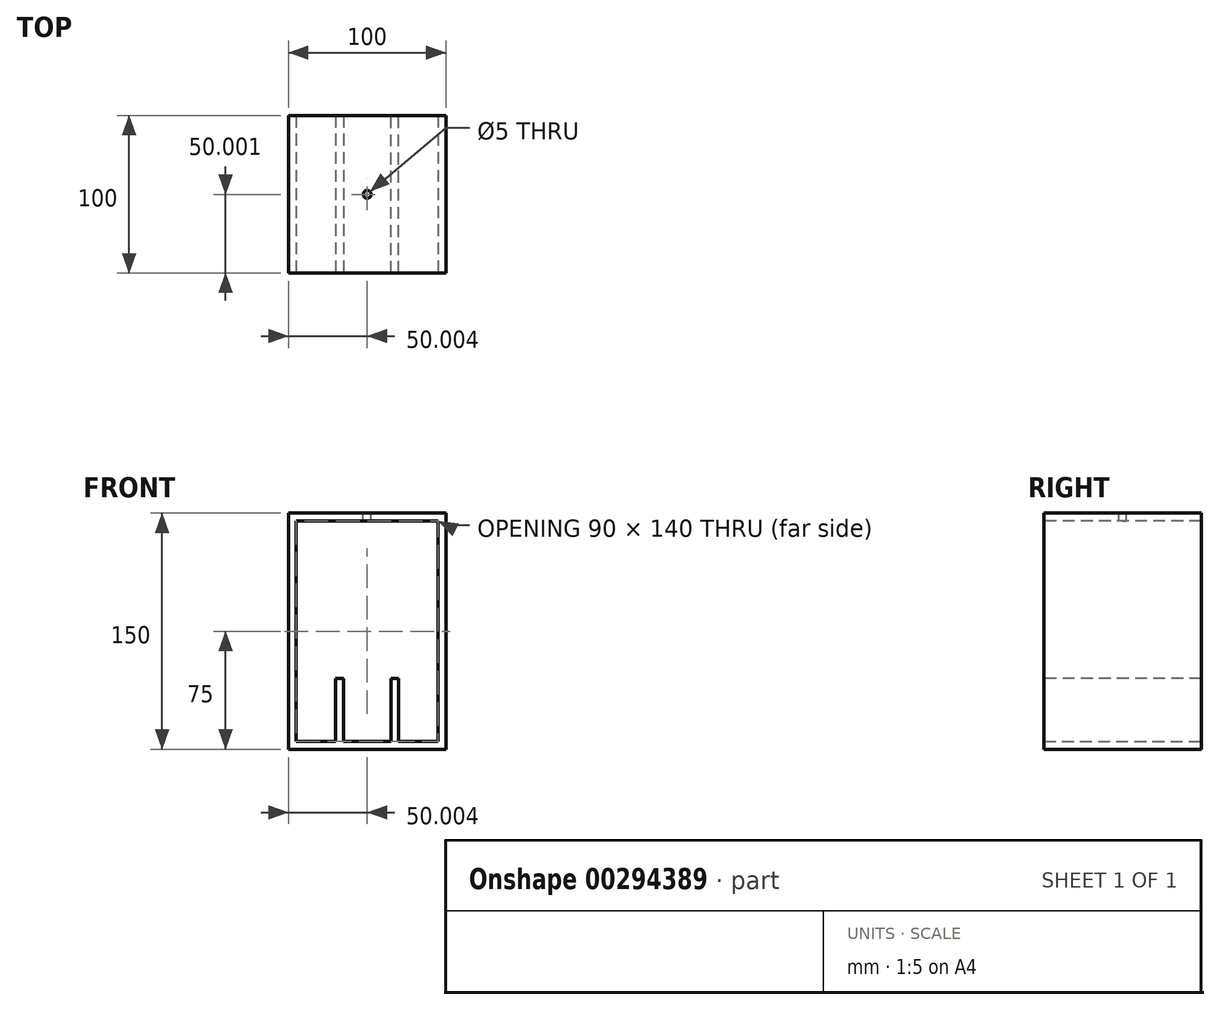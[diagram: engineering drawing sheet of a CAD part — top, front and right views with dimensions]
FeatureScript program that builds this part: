
annotation { "Feature Type Name" : "Feature", "Feature Type Description" : "" }
export const myFeature = defineFeature(function(context is Context, id is Id, definition is map)
    precondition{}
    {
        {
            var Q0;
            Q0=qCreatedBy(makeId("Top.planeOp"),FACE);
            var sketch = newSketch(context, id + "F0", { "sketchPlane" : qUnion([Q0])});
            skLineSegment(sketch, "E0.bottom", {"start": v(-54.99, 57.07) * mm, "end": v(45.01, 57.07) * mm});
            skLineSegment(sketch, "E0.top", {"start": v(-54.99, -42.93) * mm, "end": v(45.01, -42.93) * mm});
            skLineSegment(sketch, "E0.left", {"start": v(-54.99, 57.07) * mm, "end": v(-54.99, -42.93) * mm});
            skLineSegment(sketch, "E0.right", {"start": v(45.01, 57.07) * mm, "end": v(45.01, -42.93) * mm});
            skSolve(sketch);
        }
        {
            var Q0;
            Q0=makeQuery(id+"F0.imprint","IMPRINT",FACE,{"disambiguationData":[TD([[makeQuery(id+"F0.imprint","IMPRINT",EDGE,{"derivedFrom":sQuery(id+"F0.wireOp",EDGE,"E0.bottom")}),-1.0]])]});
            extrude(context, id + "F1", {"entities" : qUnion([Q0]), "depth" : 150 * mm});
        }
        {
            var Q0;
            Q0=makeQuery(id+"F1.opExtrude","SWEPT_FACE",FACE,{"disambiguationData":[OSD([sQuery(id+"F0.wireOp",EDGE,"E0.top")])]});
            var sketch = newSketch(context, id + "F2", { "sketchPlane" : qUnion([Q0])});
            skLineSegment(sketch, "E1.bottom", {"start": v(-49.99, 5) * mm, "end": v(40.01, 5) * mm});
            skLineSegment(sketch, "E1.top", {"start": v(-49.99, 145) * mm, "end": v(40.01, 145) * mm});
            skLineSegment(sketch, "E1.left", {"start": v(-49.99, 5) * mm, "end": v(-49.99, 145) * mm});
            skLineSegment(sketch, "E1.right", {"start": v(40.01, 5) * mm, "end": v(40.01, 145) * mm});
            skSolve(sketch);
        }
        {
            var Q0;
            Q0 = qSketchRegion(id + "F2", true);
            extrude(context, id + "F3", {"entities" : qUnion([Q0]), "operationType" : NewBodyOperationType.REMOVE, "oppositeDirection" : true, "depth" : 100 * mm});
        }
        {
            var Q0;
            Q0=makeQuery(id+"F1.opExtrude","CAP_FACE",FACE,{"disambiguationData":[OSD([sQuery(id+"F0.wireOp",EDGE,"E0.bottom"),sQuery(id+"F0.wireOp",EDGE,"E0.top"),sQuery(id+"F0.wireOp",EDGE,"E0.left"),sQuery(id+"F0.wireOp",EDGE,"E0.right")])],"isStart":false});
            var sketch = newSketch(context, id + "F4", { "sketchPlane" : qUnion([Q0])});
            skCircle(sketch, "E2", {"center": v(-4.99, 7.07) * mm, "radius": 2.5 * mm});
            skSolve(sketch);
        }
        {
            var Q0;
            Q0=makeQuery(id+"F4.imprint","IMPRINT",FACE,{"disambiguationData":[TD([[makeQuery(id+"F4.imprint","IMPRINT",EDGE,{"derivedFrom":sQuery(id+"F4.wireOp",EDGE,"E2")}),1.0]])]});
            extrude(context, id + "F5", {"entities" : qUnion([Q0]), "operationType" : NewBodyOperationType.REMOVE, "oppositeDirection" : true, "depth" : 50 * mm});
        }
        {
            var Q0;
            Q0=makeQuery(id+"F3.boolean.opBoolean","COPY",FACE,{"derivedFrom":makeQuery(id+"F3.opExtrude","SWEPT_FACE",FACE,{"disambiguationData":[OSD([sQuery(id+"F2.wireOp",EDGE,"E1.bottom")])]})});
            var sketch = newSketch(context, id + "F6", { "sketchPlane" : qUnion([Q0])});
            skLineSegment(sketch, "E3.bottom", {"start": v(-24.99, 57.07) * mm, "end": v(-19.99, 57.07) * mm});
            skLineSegment(sketch, "E3.top", {"start": v(-24.99, -42.93) * mm, "end": v(-19.99, -42.93) * mm});
            skLineSegment(sketch, "E3.left", {"start": v(-24.99, 57.07) * mm, "end": v(-24.99, -42.93) * mm});
            skLineSegment(sketch, "E3.right", {"start": v(-19.99, 57.07) * mm, "end": v(-19.99, -42.93) * mm});
            skLineSegment(sketch, "E4.bottom", {"start": v(10.01, -42.93) * mm, "end": v(15.01, -42.93) * mm});
            skLineSegment(sketch, "E4.top", {"start": v(10.01, 57.07) * mm, "end": v(15.01, 57.07) * mm});
            skLineSegment(sketch, "E4.left", {"start": v(10.01, -42.93) * mm, "end": v(10.01, 57.07) * mm});
            skLineSegment(sketch, "E4.right", {"start": v(15.01, -42.93) * mm, "end": v(15.01, 57.07) * mm});
            skSolve(sketch);
        }
        {
            var Q0;
            Q0 = qSketchRegion(id + "F6", true);
            extrude(context, id + "F7", {"entities" : qUnion([Q0]), "operationType" : NewBodyOperationType.ADD, "depth" : 40 * mm});
        }
    });
